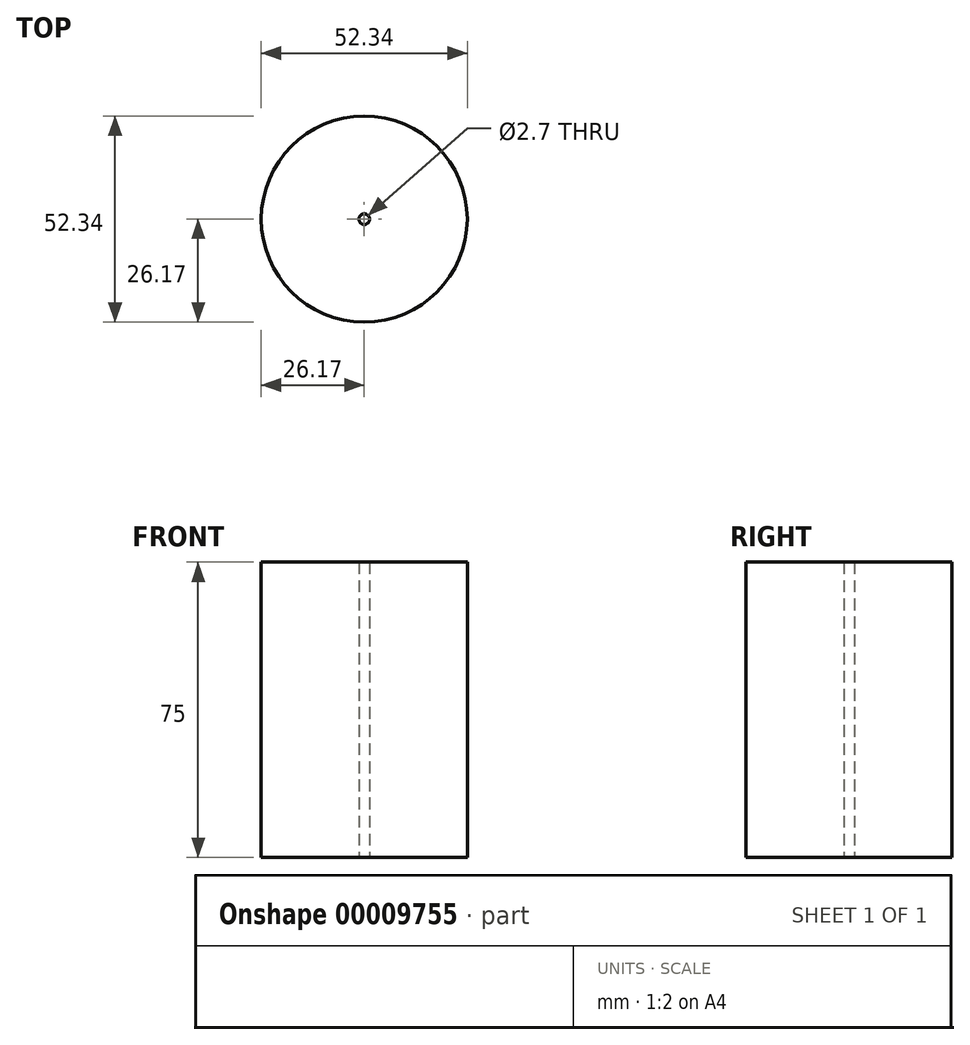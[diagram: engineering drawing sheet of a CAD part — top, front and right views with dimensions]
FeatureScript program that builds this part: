
annotation { "Feature Type Name" : "Feature", "Feature Type Description" : "" }
export const myFeature = defineFeature(function(context is Context, id is Id, definition is map)
    precondition{}
    {
        {
            var Q0;
            Q0=qCreatedBy(makeId("Top.planeOp"),FACE);
            var sketch = newSketch(context, id + "F0", { "sketchPlane" : qUnion([Q0])});
            skCircle(sketch, "E0", {"center": v(0, 0) * mm, "radius": 26.17 * mm});
            skCircle(sketch, "E1", {"center": v(0, 0) * mm, "radius": 1.35 * mm});
            skSolve(sketch);
        }
        {
            var Q0;
            Q0=makeQuery(id+"F0.imprint","IMPRINT",FACE,{"disambiguationData":[TD([[makeQuery(id+"F0.imprint","IMPRINT",EDGE,{"derivedFrom":sQuery(id+"F0.wireOp",EDGE,"E0")}),1.0]])]});
            extrude(context, id + "F1", {"entities" : qUnion([Q0]), "depth" : 75 * mm});
        }
    });
